# Revit family: Inplana_C11
name_source: partatom
category: Leuchten
revit_build: Autodesk Revit 2018 (Build: 20170223_1515(x64)
units: mm (PartAtom-declared; Revit-internal decimal feet)

## family parameters
Basisbauteil = Fläche
Beim Laden mit Abzugskörper schneiden = Nein
Bemaßung runder Anschluss = Durchmesser verwenden
Gemeinsam genutzt = Ja
Lichtquelle = Nein
OmniClass-Nummer = 23.80.70.14
OmniClass-Titel = Luminaries for External Lighting
Raumberechnungspunkt = Nein
Teiletyp = Normal

## types (1)
- Inplana_C11
    CRI = 80
    Color = white
    Colour temperature (K) = 6500
    Connection Load = 10 VA
    Degree of protection = IP20
    Dimming/Balast = - / E
    Emit Diameter = 444 mm
    Hersteller = TRILUX
    LS_offset = 7 mm  [stored 0.0229659 ft]
    Lamp_0 = Lamp
    Lampe = Lamp
    Light Source = Inplana_LS : TX057258
    Luminous flux of luminaire (lm) = 1000
    Mat = TRILUX_RAL9016
    R_1 = 222 mm
    SEO = TRILUX_WH_3000
    Safety class = I
    Scheinlast = 10 VA
    TK = 00000000
    TOC = 0000000
    URL = http://www.trilux.com
    Vorgabe-Ansicht = 0 mm  [stored 0 ft]
    Weight = 0
    h = 35 mm  [stored 0.114829 ft]
    l = 444 mm
    r2 = 210 mm  [stored 0.688976 ft]
    r3 = 208 mm
    w = 444 mm

note: [stored X ft] marks values corroborated as IEEE doubles in the binary element streams (Revit-internal decimal feet)

## geometry (parser evidence)
native form markers: Blend x22, Sweep x5
no freeform markers — native parametric forms only
